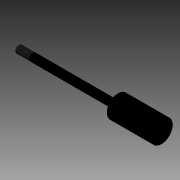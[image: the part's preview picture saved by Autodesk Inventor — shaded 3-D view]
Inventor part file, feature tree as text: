
AUTODESK INVENTOR PART (.ipt)
format: ipt  version: 2014 SP2 (Build 180246200, 246)  size: 136,704 bytes
history: native  units: in
note: dims shown in document units (in); Inventor stores cm internally (conversion verified against a paired STEP export)
features: other x70, revolve x3, sketch x3, thread x1
ambient origin geometry x8: Origin, YZ Plane, XZ Plane, XY Plane, X Axis, Y Axis, Z Axis, Center Point
bodies: Solid1 (feature_tree)
feature tree (77):
  revolve  "Revolution1"  Angle=360.0deg
  revolve  "Revolution2"  Angle=360.0deg
  thread  "Thread1"  [1 undecoded]
  revolve  "Revolution3"  [1 undecoded]
  other  "dia1_XY"
  other  "dia1_YZ"
  other  "dia1_ZX"
  other  "dia1_X"
  other  "dia1_Y"
  other  "dia1_Z"
  other  "dia1_Center"
  other  "dia12_XY"
  other  "dia12_YZ"
  other  "dia12_ZX"
  other  "dia12_X"
  other  "dia12_Y"
  other  "dia12_Z"
  other  "dia12_Center"
  other  "dia2_XY"
  other  "dia2_YZ"
  other  "dia2_ZX"
  other  "dia2_X"
  other  "dia2_Y"
  other  "dia2_Z"
  other  "dia2_Center"
  other  "dia22_XY"
  other  "dia22_YZ"
  other  "dia22_ZX"
  other  "dia22_X"
  other  "dia22_Y"
  other  "dia22_Z"
  other  "dia22_Center"
  other  "rl1_XY"
  other  "rl1_YZ"
  other  "rl1_ZX"
  other  "rl1_X"
  other  "rl1_Y"
  other  "rl1_Z"
  other  "rl1_Center"
  other  "rl2_XY"
  other  "rl2_YZ"
  other  "rl2_ZX"
  other  "rl2_X"
  other  "rl2_Y"
  other  "rl2_Z"
  other  "rl2_Center"
  other  "rod_cp_XY"
  other  "rod_cp_YZ"
  other  "rod_cp_ZX"
  other  "rod_cp_X"
  other  "rod_cp_Y"
  other  "rod_cp_Z"
  other  "rod_cp_Center"
  other  "thd1_XY"
  other  "thd1_YZ"
  other  "thd1_ZX"
  other  "thd1_X"
  other  "thd1_Y"
  other  "thd1_Z"
  other  "thd1_Center"
  other  "thd2_XY"
  other  "thd2_YZ"
  other  "thd2_ZX"
  other  "thd2_X"
  other  "thd2_Y"
  other  "thd2_Z"
  other  "thd2_Center"
  other  "to_rod_clevis_XY"
  other  "to_rod_clevis_YZ"
  other  "to_rod_clevis_ZX"
  other  "to_rod_clevis_X"
  other  "to_rod_clevis_Y"
  other  "to_rod_clevis_Z"
  other  "to_rod_clevis_Center"
  sketch  "Sketch_1"  dims[d0=360.0deg d1=360.0deg]
  sketch  "Sketch_3"  dims[d2=0.4787in d3=0.0in d4=360.0deg]
  sketch  "Sketch_30"  dims[d5=0.0in d6=0.0in d7=0.0in d8=0.0in d9=0.0in]
note: 2 required parameter values undecoded (feature->parameter linkage not recoverable at this tier; creation-order binding heuristic only, values carry confidence <= 0.55)
